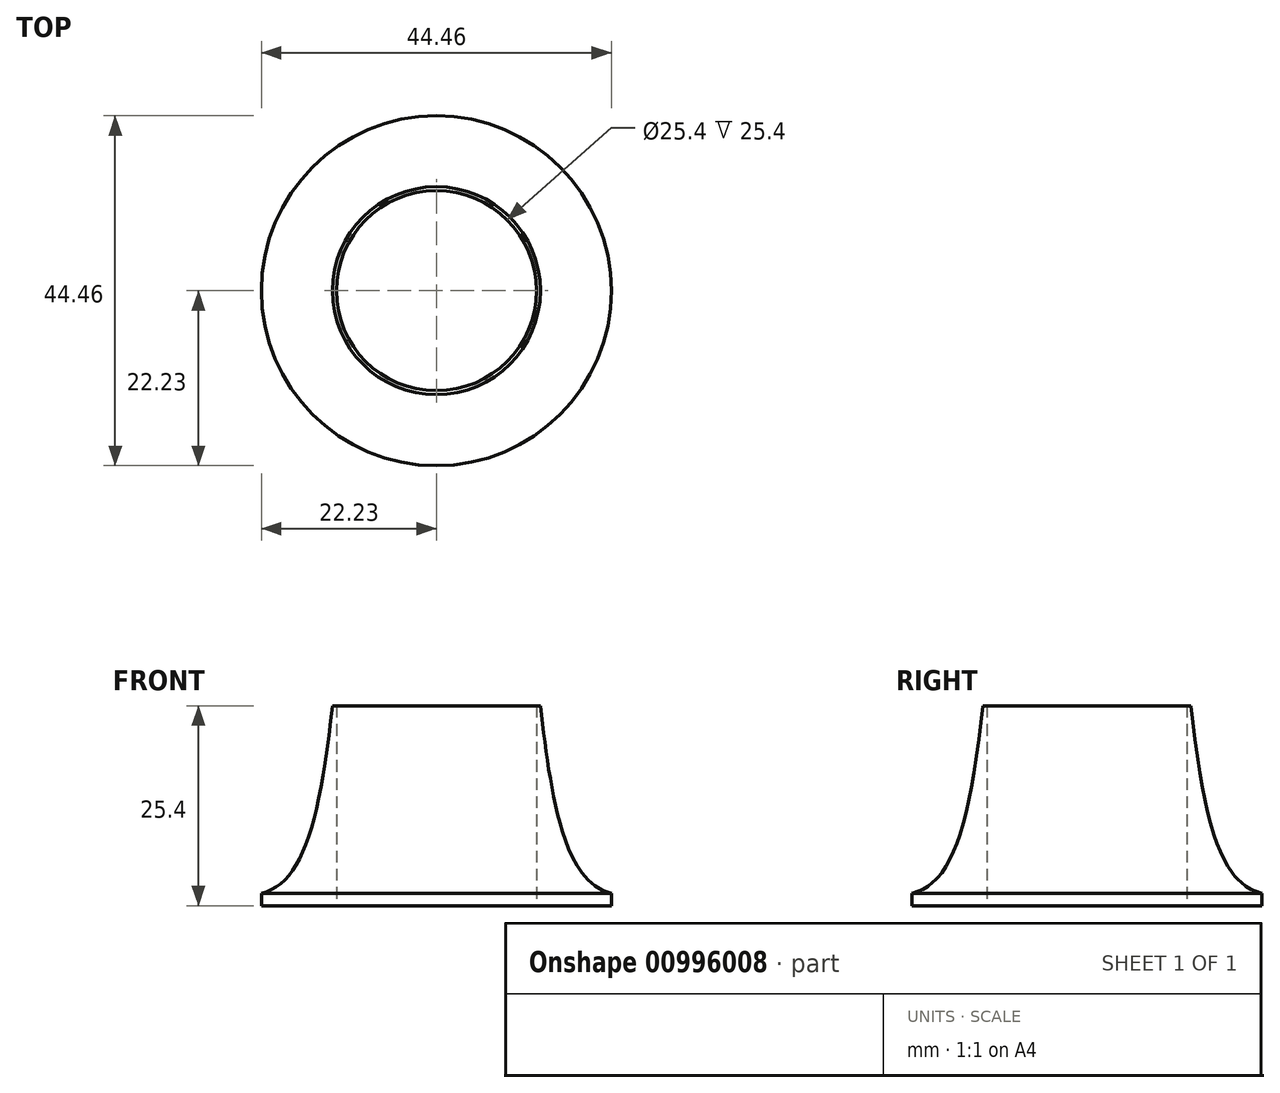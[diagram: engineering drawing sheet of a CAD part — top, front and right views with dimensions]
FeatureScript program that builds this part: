
annotation { "Feature Type Name" : "Feature", "Feature Type Description" : "" }
export const myFeature = defineFeature(function(context is Context, id is Id, definition is map)
    precondition{}
    {
        {
            var Q0;
            Q0=qCreatedBy(makeId("Front.planeOp"),FACE);
            var sketch = newSketch(context, id + "F0", { "sketchPlane" : qUnion([Q0])});
            skLineSegment(sketch, "E0", {"start": v(12.7, 0) * mm, "end": v(12.7, 25.4) * mm});
            skLineSegment(sketch, "E1", {"start": v(0, 0) * mm, "end": v(0, 56.86) * mm, "construction": true});
            skFitSpline(sketch, "E2", {"points": [v(13.2, 25.4) * mm, v(22.23, 1.59) * mm], "startDerivative": vector(5.07, -45.57) * mm, "endDerivative": vector(15.61, -3.7) * mm});
            skLineSegment(sketch, "E3", {"start": v(12.7, 0) * mm, "end": v(22.23, 0) * mm});
            skLineSegment(sketch, "E4", {"start": v(22.23, 0) * mm, "end": v(22.23, 1.59) * mm});
            skLineSegment(sketch, "E5", {"start": v(12.7, 25.4) * mm, "end": v(13.2, 25.4) * mm});
            skSolve(sketch);
        }
        {
            var Q0;
            Q0 = qSketchRegion(id + "F0", true);
            var Q1;
            Q1=sQuery(id+"F0.wireOp",EDGE,"E1");
            revolve(context, id + "F1", {"surfaceOperationType" : NewSurfaceOperationType.NEW, "entities" : qUnion([Q0]), "axis" : qUnion([Q1]), "revolveType" : RevolveType.FULL});
        }
    });
